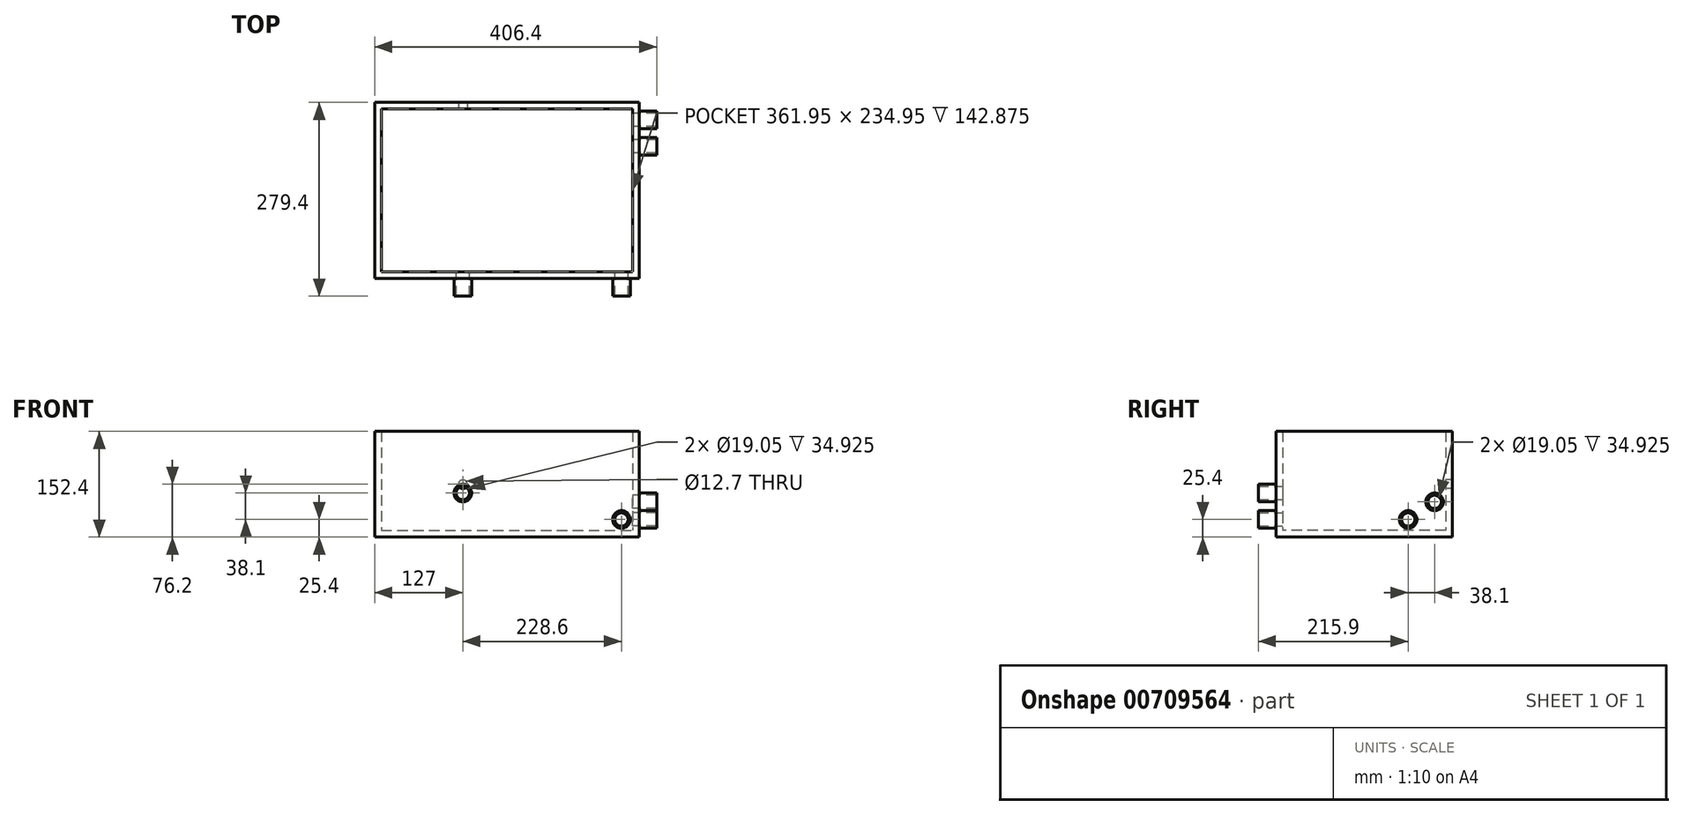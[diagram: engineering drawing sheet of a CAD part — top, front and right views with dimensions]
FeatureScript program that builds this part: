
annotation { "Feature Type Name" : "Feature", "Feature Type Description" : "" }
export const myFeature = defineFeature(function(context is Context, id is Id, definition is map)
    precondition{}
    {
        {
            var Q0;
            Q0=qCreatedBy(makeId("Top.planeOp"),FACE);
            var sketch = newSketch(context, id + "F0", { "sketchPlane" : qUnion([Q0])});
            skLineSegment(sketch, "E0.bottom", {"start": v(-190.5, 127) * mm, "end": v(190.5, 127) * mm});
            skLineSegment(sketch, "E0.top", {"start": v(-190.5, -127) * mm, "end": v(190.5, -127) * mm});
            skLineSegment(sketch, "E0.left", {"start": v(-190.5, 127) * mm, "end": v(-190.5, -127) * mm});
            skLineSegment(sketch, "E0.right", {"start": v(190.5, 127) * mm, "end": v(190.5, -127) * mm});
            skSolve(sketch);
        }
        {
            var Q0;
            Q0 = qSketchRegion(id + "F0", true);
            extrude(context, id + "F1", {"entities" : qUnion([Q0]), "depth" : 152.4 * mm, "offsetDistance" : 25.4 * mm});
        }
        {
            var Q0;
            Q0=makeQuery(id+"F1.opExtrude","CAP_FACE",FACE,{"disambiguationData":[OSD([sQuery(id+"F0.wireOp",EDGE,"E0.bottom"),sQuery(id+"F0.wireOp",EDGE,"E0.top"),sQuery(id+"F0.wireOp",EDGE,"E0.left"),sQuery(id+"F0.wireOp",EDGE,"E0.right")])],"isStart":false});
            shell(context, id + "F2", {"entities" : qUnion([Q0]), "thickness" : 9.52 * mm});
        }
        {
            var Q0;
            Q0=makeQuery(id+"F1.opExtrude","SWEPT_FACE",FACE,{"disambiguationData":[OSD([sQuery(id+"F0.wireOp",EDGE,"E0.right")])]});
            var sketch = newSketch(context, id + "F3", { "sketchPlane" : qUnion([Q0])});
            skCircle(sketch, "E1", {"center": v(63.5, 25.4) * mm, "radius": 9.53 * mm});
            skCircle(sketch, "E2", {"center": v(63.5, 25.4) * mm, "radius": 12.7 * mm});
            skCircle(sketch, "E3", {"center": v(101.6, 50.8) * mm, "radius": 9.53 * mm});
            skCircle(sketch, "E4", {"center": v(101.6, 50.8) * mm, "radius": 12.7 * mm});
            skSolve(sketch);
        }
        {
            var Q0;
            Q0 = qSketchRegion(id + "F3", true);
            extrude(context, id + "F4", {"entities" : qUnion([Q0]), "operationType" : NewBodyOperationType.ADD, "depth" : 25.4 * mm, "offsetDistance" : 25.4 * mm});
        }
        {
            var Q0;
            Q0=makeQuery(id+"F4.boolean.opBoolean","SPLIT",FACE,{"disambiguationData":[TD([makeQuery(id+"F4.opExtrude","SWEPT_FACE",FACE,{"disambiguationData":[OSD([sQuery(id+"F3.wireOp",EDGE,"E1")])]})])],"derivedFrom":makeQuery(id+"F1.opExtrude","SWEPT_FACE",FACE,{"disambiguationData":[OSD([sQuery(id+"F0.wireOp",EDGE,"E0.right")])]})});
            var sketch = newSketch(context, id + "F5", { "sketchPlane" : qUnion([Q0])});
            skCircle(sketch, "E5.0", {"center": v(63.5, 25.4) * mm, "radius": 9.53 * mm});
            skCircle(sketch, "E6.0", {"center": v(101.6, 50.8) * mm, "radius": 9.53 * mm});
            skSolve(sketch);
        }
        {
            var Q0;
            Q0 = qSketchRegion(id + "F5", true);
            extrude(context, id + "F6", {"entities" : qUnion([Q0]), "operationType" : NewBodyOperationType.REMOVE, "endBound" : BoundingType.UP_TO_NEXT, "oppositeDirection" : true, "depth" : 25.4 * mm, "offsetDistance" : 25.4 * mm});
        }
        {
            var Q0;
            Q0=makeQuery(id+"F1.opExtrude","SWEPT_FACE",FACE,{"disambiguationData":[OSD([sQuery(id+"F0.wireOp",EDGE,"E0.top")])]});
            var sketch = newSketch(context, id + "F7", { "sketchPlane" : qUnion([Q0])});
            skCircle(sketch, "E7", {"center": v(-63.5, 63.5) * mm, "radius": 12.7 * mm});
            skCircle(sketch, "E8", {"center": v(-63.5, 63.5) * mm, "radius": 9.53 * mm});
            skCircle(sketch, "E9", {"center": v(165.1, 25.4) * mm, "radius": 9.53 * mm});
            skCircle(sketch, "E10", {"center": v(165.1, 25.4) * mm, "radius": 12.7 * mm});
            skSolve(sketch);
        }
        {
            var Q0;
            Q0 = qSketchRegion(id + "F7", true);
            extrude(context, id + "F8", {"entities" : qUnion([Q0]), "operationType" : NewBodyOperationType.ADD, "depth" : 25.4 * mm, "offsetDistance" : 25.4 * mm});
        }
        {
            var Q0;
            {var subQ1=sQuery(id+"F0.wireOp",EDGE,"E0.left");var subQ2=sQuery(id+"F0.wireOp",EDGE,"E0.top");Q0=makeQuery(id+"F8.boolean.opBoolean","SPLIT",FACE,{"disambiguationData":[TD([makeQuery(id+"F1.opExtrude","SWEPT_FACE",FACE,{"disambiguationData":[OSD([subQ1])]})])],"derivedFrom":makeQuery(id+"F1.opExtrude","SWEPT_FACE",FACE,{"disambiguationData":[OSD([subQ2])]})});}
            var sketch = newSketch(context, id + "F9", { "sketchPlane" : qUnion([Q0])});
            skCircle(sketch, "E11.0", {"center": v(-63.5, 63.5) * mm, "radius": 9.53 * mm});
            skCircle(sketch, "E12.0", {"center": v(165.1, 25.4) * mm, "radius": 9.53 * mm});
            skSolve(sketch);
        }
        {
            var Q0;
            Q0 = qSketchRegion(id + "F9", true);
            extrude(context, id + "F10", {"entities" : qUnion([Q0]), "operationType" : NewBodyOperationType.REMOVE, "endBound" : BoundingType.UP_TO_NEXT, "oppositeDirection" : true, "depth" : 25.4 * mm, "offsetDistance" : 25.4 * mm});
        }
        {
            var Q0;
            Q0=makeQuery(id+"F2.opShell","OFFSET_FACE",FACE,{"disambiguationData":[OSD([sQuery(id+"F0.wireOp",EDGE,"E0.bottom")])]});
            var sketch = newSketch(context, id + "F11", { "sketchPlane" : qUnion([Q0])});
            skCircle(sketch, "E13", {"center": v(-63.5, 76.2) * mm, "radius": 6.35 * mm});
            skSolve(sketch);
        }
        {
            var Q0;
            Q0 = qSketchRegion(id + "F11", true);
            extrude(context, id + "F12", {"entities" : qUnion([Q0]), "operationType" : NewBodyOperationType.REMOVE, "oppositeDirection" : true, "depth" : 25.4 * mm, "offsetDistance" : 25.4 * mm});
        }
    });
